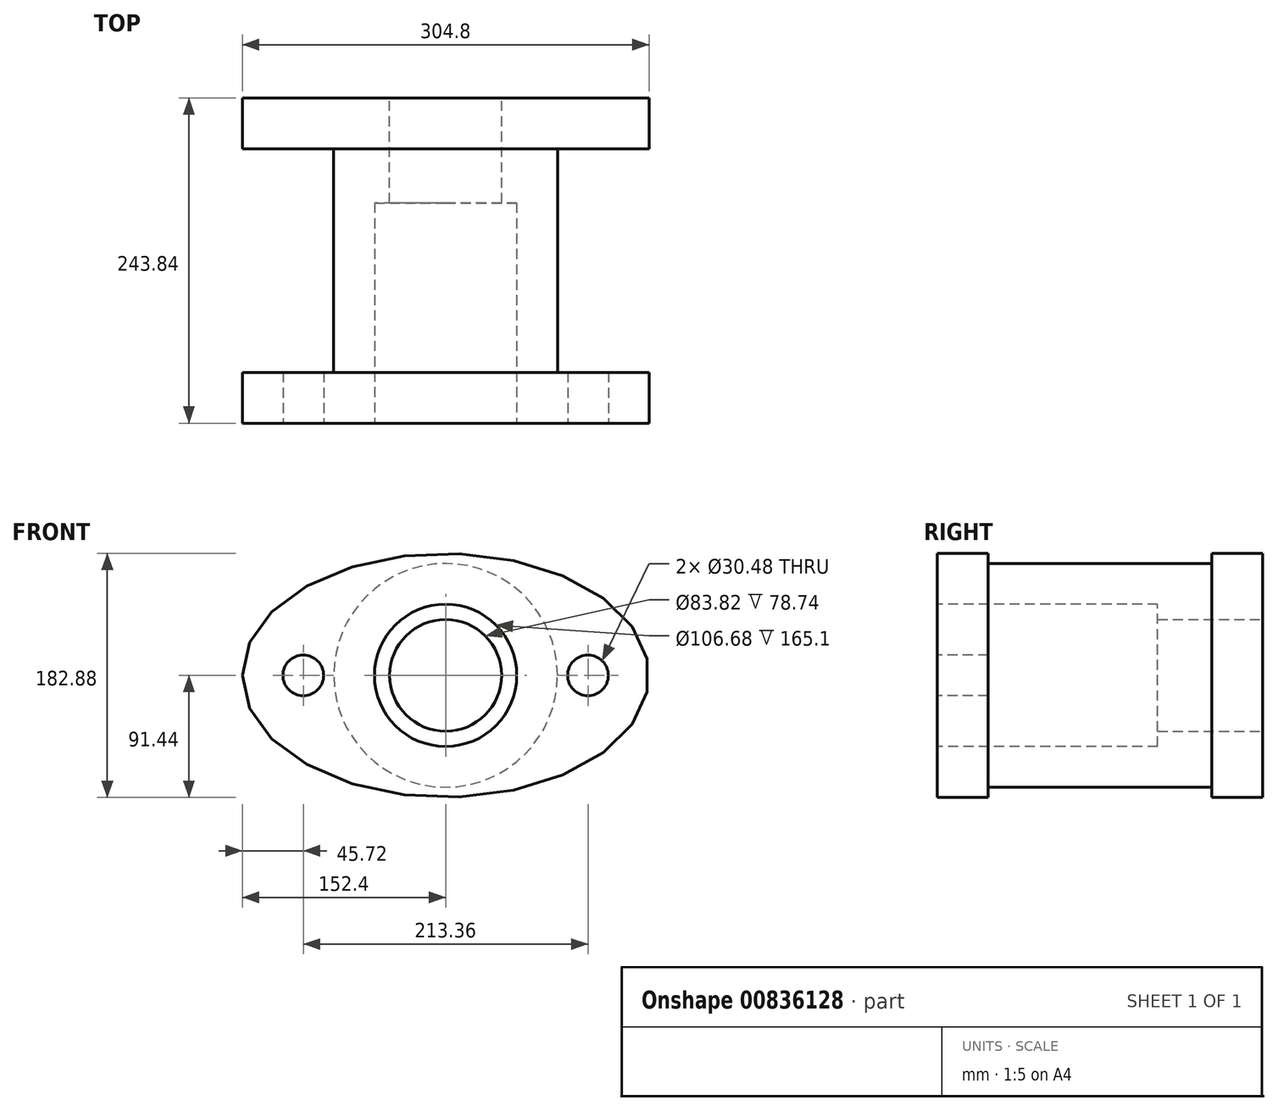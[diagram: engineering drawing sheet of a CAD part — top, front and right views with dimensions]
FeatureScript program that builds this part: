
annotation { "Feature Type Name" : "Feature", "Feature Type Description" : "" }
export const myFeature = defineFeature(function(context is Context, id is Id, definition is map)
    precondition{}
    {
        {
            var Q0;
            Q0=qCreatedBy(makeId("Front.planeOp"),FACE);
            var sketch = newSketch(context, id + "F0", { "sketchPlane" : qUnion([Q0])});
            skEllipse(sketch, "E0", {"center": v(0, 0) * mm, "majorRadius": 152.4 * mm, "minorRadius": 91.44 * mm, "majorAxis": v(-1, 0)});
            skSolve(sketch);
        }
        {
            var Q0;
            Q0=makeQuery(id+"F0.imprint","IMPRINT",FACE,{"disambiguationData":[TD([[makeQuery(id+"F0.imprint","IMPRINT",EDGE,{"derivedFrom":sQuery(id+"F0.wireOp",EDGE,"E0")}),1.0]])]});
            extrude(context, id + "F1", {"entities" : qUnion([Q0]), "depth" : 38.1 * mm, "offsetDistance" : 25.4 * mm});
        }
        {
            var Q0;
            Q0=makeQuery(id+"F1.opExtrude","CAP_FACE",FACE,{"disambiguationData":[OSD([sQuery(id+"F0.wireOp",EDGE,"E0")])],"isStart":false});
            var sketch = newSketch(context, id + "F2", { "sketchPlane" : qUnion([Q0])});
            skCircle(sketch, "E1", {"center": v(-106.68, 0) * mm, "radius": 15.24 * mm});
            skCircle(sketch, "E2", {"center": v(106.68, 0) * mm, "radius": 15.24 * mm});
            skSolve(sketch);
        }
        {
            var Q0;
            Q0=makeQuery(id+"F2.imprint","IMPRINT",FACE,{"disambiguationData":[TD([[makeQuery(id+"F2.imprint","IMPRINT",EDGE,{"derivedFrom":sQuery(id+"F2.wireOp",EDGE,"E1")}),1.0]])]});
            var Q1;
            Q1=makeQuery(id+"F2.imprint","IMPRINT",FACE,{"disambiguationData":[TD([[makeQuery(id+"F2.imprint","IMPRINT",EDGE,{"derivedFrom":sQuery(id+"F2.wireOp",EDGE,"E2")}),1.0]])]});
            extrude(context, id + "F3", {"entities" : qUnion([Q0, Q1]), "operationType" : NewBodyOperationType.REMOVE, "endBound" : BoundingType.UP_TO_NEXT, "oppositeDirection" : true, "depth" : 25.4 * mm, "offsetDistance" : 25.4 * mm});
        }
        {
            var Q0;
            Q0=makeQuery(id+"F1.opExtrude","CAP_FACE",FACE,{"disambiguationData":[OSD([sQuery(id+"F0.wireOp",EDGE,"E0")])],"isStart":true});
            var sketch = newSketch(context, id + "F4", { "sketchPlane" : qUnion([Q0])});
            skCircle(sketch, "E3", {"center": v(0, 0) * mm, "radius": 83.82 * mm});
            skSolve(sketch);
        }
        {
            var Q0;
            Q0=makeQuery(id+"F4.imprint","IMPRINT",FACE,{"disambiguationData":[TD([[makeQuery(id+"F4.imprint","IMPRINT",EDGE,{"derivedFrom":sQuery(id+"F4.wireOp",EDGE,"E3")}),1.0]])]});
            extrude(context, id + "F5", {"entities" : qUnion([Q0]), "operationType" : NewBodyOperationType.ADD, "depth" : 167.64 * mm, "offsetDistance" : 25.4 * mm});
        }
        {
            var Q0;
            Q0=makeQuery(id+"F5.opExtrude","CAP_FACE",FACE,{"disambiguationData":[OSD([sQuery(id+"F4.wireOp",EDGE,"E3")])],"isStart":false});
            var sketch = newSketch(context, id + "F6", { "sketchPlane" : qUnion([Q0])});
            skEllipse(sketch, "E4", {"center": v(0, 0) * mm, "majorRadius": 152.4 * mm, "minorRadius": 91.44 * mm, "majorAxis": v(1, 0)});
            skSolve(sketch);
        }
        {
            var Q0;
            Q0 = qSketchRegion(id + "F6", true);
            extrude(context, id + "F7", {"entities" : qUnion([Q0]), "operationType" : NewBodyOperationType.ADD, "depth" : 38.1 * mm, "offsetDistance" : 25.4 * mm});
        }
        {
            var Q0;
            Q0=makeQuery(id+"F7.opExtrude","CAP_FACE",FACE,{"disambiguationData":[OSD([sQuery(id+"F6.wireOp",EDGE,"E4")])],"isStart":false});
            var sketch = newSketch(context, id + "F8", { "sketchPlane" : qUnion([Q0])});
            skCircle(sketch, "E5", {"center": v(0, 0) * mm, "radius": 41.91 * mm});
            skSolve(sketch);
        }
        {
            var Q0;
            Q0 = qSketchRegion(id + "F8", true);
            extrude(context, id + "F9", {"entities" : qUnion([Q0]), "operationType" : NewBodyOperationType.REMOVE, "endBound" : BoundingType.UP_TO_NEXT, "oppositeDirection" : true, "depth" : 25.4 * mm, "offsetDistance" : 25.4 * mm});
        }
        {
            var Q0;
            Q0=makeQuery(id+"F1.opExtrude","CAP_FACE",FACE,{"disambiguationData":[OSD([sQuery(id+"F0.wireOp",EDGE,"E0")])],"isStart":false});
            var sketch = newSketch(context, id + "F10", { "sketchPlane" : qUnion([Q0])});
            skCircle(sketch, "E6", {"center": v(0, 0) * mm, "radius": 53.34 * mm});
            skSolve(sketch);
        }
        {
            var Q0;
            Q0 = qSketchRegion(id + "F10", true);
            extrude(context, id + "F11", {"entities" : qUnion([Q0]), "operationType" : NewBodyOperationType.REMOVE, "oppositeDirection" : true, "depth" : 165.1 * mm, "offsetDistance" : 25.4 * mm});
        }
    });
